# Revit family: Multibrand_Oleas_Multuproduct_BIM_NN_ASH;IS;POR;P0117;R0119;R0121;R0122;R0182;S0767
name_source: partatom
category: Plumbing Fixtures
revit_build: Autodesk Revit 2017 (Build: 20160225_1515(x64)
units: mm (PartAtom-declared; Revit-internal decimal feet)

## family parameters
Cut with Voids When Loaded = No
Host = Face
OmniClass Number = 23.45.05.21.11.11
OmniClass Title = Water Operated Water Closets
Part Type = Normal
Room Calculation Point = No
Round Connector Dimension = Use Diameter
Shared = Yes

## types (7) — shared parameters
Accesoires = https://www.idealstandard.de
AfstandsEenheid = Millimeter
Assembly Code = C1030200
Auteur = Ideal Standrad
Beschrijvinggarantie = Garantie van de fabrikant
Douchebak = No
DuurEenheid = Jaren
Garantieonderdelen = 5
Garantieunits = Jaren
Heefthandvaten = No
Hulp = https://www.idealstandard.de
Installatieinstructies = https://www.idealstandard.de
Manufacturer = https://www.idealstandard.de
Materiaal = Metall
Merk = Ideal Standard
Montageinstuctie = https://www.idealstandard.de
NBSDescription = WC cistern flush pipes
NBSReference = 45-35-70/388
Productinformatie = https://www.idealstandard.de
Revisie = 1
Revision = 1
Telefoonnummer = 0049 228 5210
URL = https://www.idealstandard.de
Uniclass2 = Pr_40_20_93_89
Uniclass2015Beschrijving = WC cistern flush pipes
Uniclass2015Description = WC cistern flush pipes
Uniclass2015Reference = Pr_40_20_93_90
Uniclass2015Referentie = Pr_40_20_93_90
Urlproducent = https://www.idealstandard.de
Versie = 1
Verwachtelevensduur = 25
Volumeunits = liter
WRAS = No
WaterEfficientProduct = No
zero-valued in all types: Breedte, BrutoGewicht, CWFU, Cost, Default Elevation, GrootteAfvoergat, HWFU, Lengte, Nettogewicht, Overloop, Vervangingskosten, WFU

## per-type parameters (varying)
| type | Afmetingen | Afwerking | Artikelnummer | Artikelomschrijving | Artikelreferentie | Barcode | BimObjectNaam | Description | Diepte | Eigenschappen | Hoogte | Kleur | Model | Normen | Referentie |
| R0117AC - OLEAS P2 F/PLATE WHITE - PO | 160 x 245 x 17 mm | White | R0117AC | OLEAS M1 ENKELE BEDIENINGSBORD WIT | OLEAS M1 ENKELE BEDIENINGSBORD WIT | 3391500580206 | IS_IdealStandard_WCcisternflushpipes_Oleas_R0117 | OLEAS M1 ENKELE BEDIENINGSBORD WIT | 245 mm  [stored 0.803806 ft] | OLEAS M1 ENKELE BEDIENINGSBORD WIT | 160 | Weiß | R0117AC | WCcisternflushpipes_Oleas_R0117_IdealStandard | R0117AC |
| R0119AA - OLEAS P2 F/PLATE DUAL CHROME - IS | 98 x 188, 265 x 260, 190 mm | Chrome | R0119AA | Betätigungsplatte P2 OLEAS. pneumatischen Auslösung. Chrom | Betätigungsplatte P2 OLEAS. pneumatischen Auslösung. Chrom | 3391500580251 | IS_IdealStandard_WCcisternflushpipes_Oleas_R0119 | Betätigungsplatte P2 OLEAS. pneumatischen Auslösung. Chrom | 0 mm  [stored 0 ft] | Betätigungsplatte P2 OLEAS. pneumatischen Auslösung. Chrom | 98 | Chrom | R0119AA | WCcisternflushpipes_Oleas_R0119_IdealStandard | R0119AA |
| R0121AA - OLEAS M2 F/PLATE DUAL CHROME - IS | 55 x 265, 245 x 190, 17 mm | Chrome | R0121AA | Betätigungsplatte M2 OLEAS. mechanischen Auslösung. Chrom | Betätigungsplatte M2 OLEAS. mechanischen Auslösung. Chrom | 3391500580329 | IS_IdealStandard_WCcisternflushpipes_Oleas_R0121 | Betätigungsplatte M2 OLEAS. mechanischen Auslösung. Chrom | 0 mm  [stored 0 ft] | Betätigungsplatte M2 OLEAS. mechanischen Auslösung. Chrom | 55 | Chrom | R0121AA | WCcisternflushpipes_Oleas_R0121_IdealStandard | R0121AA |
| R0122AA - OLEAS M2 F/PLATE CHROME SM/FLSH - IS | 160 x 245 x 17 mm | Chrome | R0122AA | Betätigungsplatte M2 OLEAS. SmartFlush. Chrom | Betätigungsplatte M2 OLEAS. SmartFlush. Chrom | 3391500580350 | IS_IdealStandard_WCcisternflushpipes_Oleas_R0122 | Betätigungsplatte M2 OLEAS. SmartFlush. Chrom | 245 mm  [stored 0.803806 ft] | Betätigungsplatte M2 OLEAS. SmartFlush. Chrom | 160 | Chrom | R0122AA | WCcisternflushpipes_Oleas_R0122_IdealStandard | R0122AA |
| R0182AA - OLEAS P2 F/PLATE DUAL CHROME - UNBRND | 55 x 265 x 190 mm | Chrome | R0182AA | OLEAS ™ SMARTFLUSH M2 STEUERPLATTE CHROM | OLEAS ™ SMARTFLUSH M2 STEUERPLATTE CHROM | 3391500581197 | IS_IdealStandard_WCcisternflushpipes_Oleas_R0182 | OLEAS ™ SMARTFLUSH M2 STEUERPLATTE CHROM | 265 mm  [stored 0.869423 ft] | SMARTFLUSH M2 STEUERPLATTE CHROM | 55 | Chrom | R0182AA | WCcisternflushpipes_Oleas_R0182_IdealStandard | R0182AA |
| R0182JG - OLEAS P2 F/PLATE DUAL MATT CHR - UNBRND | 55 x 265 x 190 mm | Matt Chrome | R0182JG | OLEAS ™ SMARTFLUSH M2 STEUERPLATTE MATT CHROM | OLEAS ™ SMARTFLUSH M2 STEUERPLATTE MATT CHROM | 3391500581203 | IS_IdealStandard_WCcisternflushpipes_Oleas_R0182 | OLEAS ™ SMARTFLUSH M2 STEUERPLATTE MATT CHROM | 265 mm  [stored 0.869423 ft] | SMARTFLUSH M2 STEUERPLATTE MATT CHROM | 55 | Mat chroom | R0182JG | WCcisternflushpipes_Oleas_R0182_IdealStandard | R0182JG |
| S0767AA - OLEAS M2 F/PLATE DUAL CHROME - AS | 57 x 189 x 265 mm | Chrome | S0767AA | Oleas M2 mechanische Doppelspülplatte Armitage Shanks - Chrom | Oleas M2 mechanische Doppelspülplatte Armitage Shanks - Chrom | 3391500580350 | IS_IdealStandard_WCcisternflushpipes_Oleas_S0767 | Oleas M2 mechanische Doppelspülplatte Armitage Shanks - Chrom | 189 mm  [stored 0.620079 ft] | Oleas M2 mechanische Doppelspülplatte Armitage Shanks - Chrom | 57 | Chrom | S0767AA | WCcisternflushpipes_Oleas_S0767_IdealStandard | S0767AA |

note: [stored X ft] marks values corroborated as IEEE doubles in the binary element streams (Revit-internal decimal feet)

## geometry (parser evidence)
native form markers: Sweep x3
no freeform markers — native parametric forms only
